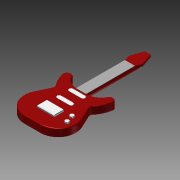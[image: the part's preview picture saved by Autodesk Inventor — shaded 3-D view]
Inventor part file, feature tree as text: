
AUTODESK INVENTOR PART (.ipt)
format: ipt  version: 2015 (Build 190159000, 159)  size: 338,432 bytes
history: native  units: mm
features: sketch x9, extrude x8, fillet x4, revolve x1
ambient origin geometry x8: Origin, YZ Plane, XZ Plane, XY Plane, X Axis, Y Axis, Z Axis, Center Point
bodies: Solid1 (feature_tree), Solid2 (feature_tree), Solid3 (feature_tree), Solid4 (feature_tree), Solid5 (feature_tree)
feature tree (22):
  extrude  "Extrusion1"  Depth=12.0mm TaperAngle=0.0deg
  extrude  "Extrusion2"  Depth=4.5mm
  extrude  "Extrusion3"  Depth=1.5mm
  revolve  "Revolution2"  [1 undecoded]
  extrude  "Extrusion4"  Depth=5.0mm
  fillet  "Fillet7"  [1 undecoded]
  extrude  "Extrusion6"  Depth=1.0mm
  extrude  "Extrusion7"  Depth=8.5mm
  extrude  "Extrusion8"  Depth=2.5mm
  fillet  "Fillet8"  Radius=5.5mm
  fillet  "Fillet9"  Radius=8.0mm
  extrude  "Extrusion9"  Depth=2.0mm
  fillet  "Fillet10"  Radius=2.0mm
  sketch  "Sketch1"  dims[d0=2.5mm d2=12.0mm d3=0.0mm]
  sketch  "Sketch3"  dims[d8=0.5mm d9=4.5mm]
  sketch  "Sketch5"  dims[d10=3.5mm d11=1.5mm]
  sketch  "Sketch6"  dims[d12=1.5mm d13=0.5mm d14=0.0mm]
  sketch  "Sketch7"  dims[d18=0.5mm d19=0.0mm d20=5.0mm d21=90.0deg]
  sketch  "Sketch10"  dims[d25=3.5mm d26=1.0mm]
  sketch  "Sketch11"  dims[d27=1.5mm d28=8.5mm]
  sketch  "Sketch12"  dims[d29=1.0mm d30=2.5mm d32=5.5mm d34=8.0mm]
  sketch  "Sketch13"  dims[d35=4.5mm d36=2.0mm d37=2.0mm d38=0.0mm d49=0.25mm d50=0.1mm d51=0.0mm d52=3.0mm d53=1.0mm d54=11.0mm d55=20.0mm d57=3.0mm d58=10.0mm d60=10.0mm d62=0.1mm d63=0.0mm d64=4.5mm d65=2.5mm d66=0.4mm d67=0.0mm d68=0.25mm d69=0.25mm d70=1.0mm d71=0.4mm d72=0.0mm d73=0.1mm]
note: 2 required parameter values undecoded (feature->parameter linkage not recoverable at this tier; creation-order binding heuristic only, values carry confidence <= 0.55)